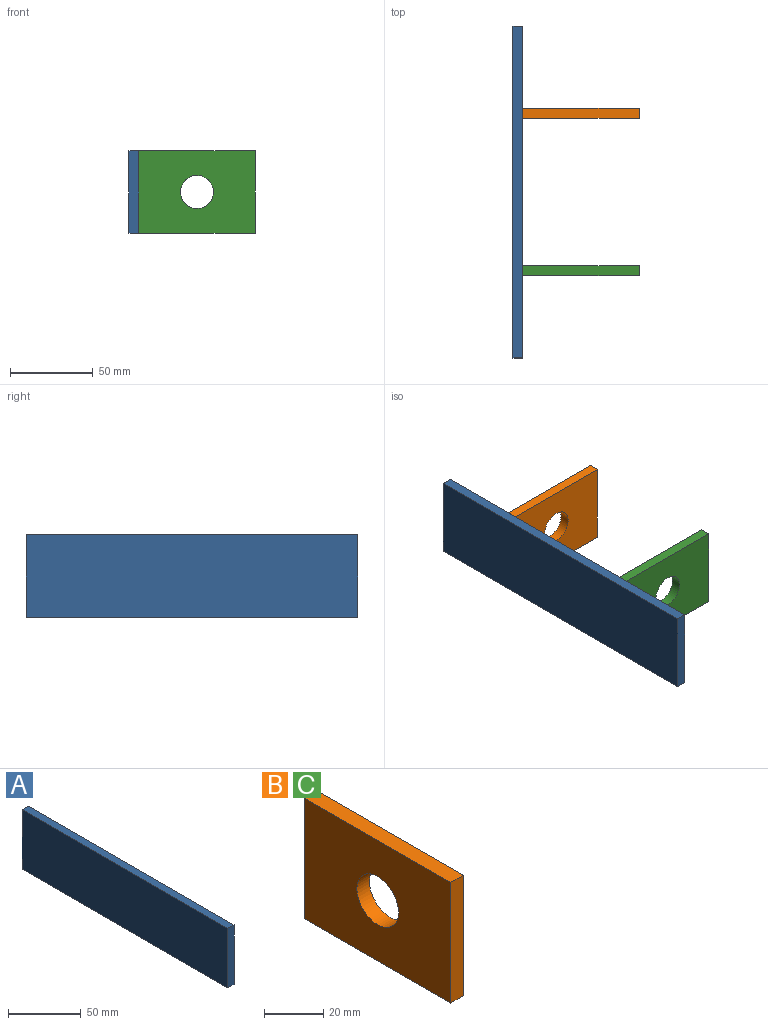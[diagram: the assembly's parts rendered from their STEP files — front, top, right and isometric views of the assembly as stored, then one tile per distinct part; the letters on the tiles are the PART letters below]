
ASSEMBLY  parts=3 mates=2
PART A: 6 faces, bbox 6x200x50 mm
  f0: plane 50x6mm, normal (0,-1,0), area 300mm2, adj f1,f3,f4,f5
  f1: plane 200x6mm, normal (0,0,1), area 1200mm2, adj f0,f2,f4,f5
  f2: plane 50x6mm, normal (0,1,0), area 300mm2, adj f1,f3,f4,f5
  f3: plane 200x6mm, normal (0,0,-1), area 1200mm2, adj f0,f2,f4,f5
  f4: plane 200x50mm, normal (-1,0,0), area 10000mm2, adj f0,f1,f2,f3
  f5: plane 200x50mm, normal (1,0,0), area 10000mm2, adj f0,f1,f2,f3
PART B: 7 faces, bbox 6x70x50 mm
  f0: plane 50x6mm, normal (0,1,0), area 300mm2, adj f1,f3,f5,f6
  f1: plane 70x6mm, normal (0,0,1), area 420mm2, adj f0,f2,f5,f6
  f2: plane 50x6mm, normal (0,-1,0), area 300mm2, adj f1,f3,f5,f6
  f3: plane 70x6mm, normal (0,0,-1), area 420mm2, adj f0,f2,f5,f6
  f4: cylinder r=10mm len=20mm, axis (-1,0,0), area 377mm2, adj f5,f6
  f5: plane 70x50mm, normal (1,0,0), area 3185.8mm2, adj f0,f1,f2,f3,f4
  f6: plane 70x50mm, normal (-1,0,0), area 3185.8mm2, adj f0,f1,f2,f3,f4
PART C: same geometry as B
PLACE A t=(-36.78,22.92,-37.02)mm
PLACE B rot(axis=(0,0,-1),90deg) t=(-133.25,-35.03,20)mm
PLACE C rot(axis=(0.71,0.71,0),180deg) t=(-133.25,-136.03,20)mm
MATE fastened B.f2 <-> A.f5  axis (-1,0,0) through (-168.25,-35.03,20)mm
MATE fastened C.f2 <-> A.f5  axis (-1,0,0) through (-168.25,-136.03,20)mm
